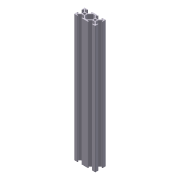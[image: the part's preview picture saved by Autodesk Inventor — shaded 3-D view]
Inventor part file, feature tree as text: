
AUTODESK INVENTOR PART (.ipt)
format: ipt  version: 2014 (Build 180170000, 170)  size: 576,000 bytes
history: native  units: mm
features: other x12, fillet x5, extrude x3, sketch x3, pattern_circular x1, mirror x1
ambient origin geometry x8: Origin, YZ Plane, XZ Plane, XY Plane, X Axis, Y Axis, Z Axis, Center Point
bodies: Solid1 (feature_tree)
feature tree (25):
  other  "Table"
  other  "Length = 50 mm"
  other  "Length = 75"
  other  "Length = 100"
  other  "Length = 150 mm"
  other  "Length = 200 mm"
  other  "Length = 250 mm"
  other  "Length = 300 mm"
  other  "Length = 350mm"
  other  "Length = 375 mm"
  other  "Length = 400 mm"
  other  "Length = 425 mm"
  extrude  "Extrusion1"  Depth=8.76mm
  extrude  "Extrusion2"  Depth=12.5mm
  pattern_circular  "Circular Pattern1"  [2 undecoded]
  mirror  "Mirror1"
  extrude  "Extrusion3"  Depth=2.14mm
  fillet  "Fillet4"  Radius=200.0mm
  fillet  "Fillet5"  Radius=40.0mm
  fillet  "Fillet6"  Radius=10.0mm
  fillet  "Fillet7"  Radius=1.0mm
  fillet  "Fillet8"  Radius=0.75mm
  sketch  "Sketch1"  dims[d0=8.76mm d1=5.0mm]
  sketch  "Sketch2"  dims[d3=0.0mm d4=12.5mm]
  sketch  "Sketch3"  dims[d5=2.14mm d6=8.1mm d7=2.14mm d8=200.0mm d9=0.0mm d10=40.0mm d11=360.0deg d16=10.0mm d17=0.0mm d18=1.0mm d19=0.75mm d20=0.75mm d21=0.75mm d22=0.75mm]
note: 2 required parameter values undecoded (feature->parameter linkage not recoverable at this tier; creation-order binding heuristic only, values carry confidence <= 0.55)
